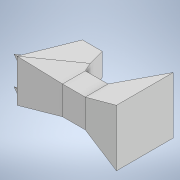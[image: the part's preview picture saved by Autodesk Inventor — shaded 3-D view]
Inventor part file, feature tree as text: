
AUTODESK INVENTOR PART (.ipt)
format: ipt  version: 2021 (Build 250183000, 183)  size: 184,320 bytes
history: native  units: in
note: dims shown in document units (in); Inventor stores cm internally (conversion verified against a paired STEP export)
features: sketch x5, extrude x3, plane x3, projected_geometry x2, loft x1, mirror x1
ambient origin geometry x8: Origin, YZ Plane, XZ Plane, XY Plane, X Axis, Y Axis, Z Axis, Center Point
bodies: Solid1 (feature_tree)
feature tree (15):
  extrude  "Extrusion1"  Depth=1.5748in
  extrude  "Extrusion2"  Depth=0.3937in
  plane  "Work Plane1"
  extrude  "Extrusion4"  Depth=1.0236in
  sketch  "Sketch5"  dims[d11=0.315in d12=0.1969in]
  plane  "Work Plane3"
  loft  "Loft3"
  plane  "Work Plane4"
  mirror  "Mirror1"
  sketch  "Sketch1"  dims[d1=1.5748in d2=0.7874in]
  sketch  "Sketch2"  dims[d7=0.3937in d8=1.4567in]
  projected_geometry  "Projected Loop1"
  sketch  "Sketch4"  dims[d9=0.2756in d10=1.0236in]
  projected_geometry  "Projected Loop2"
  sketch  "Sketch8"  dims[d13=0.7874in d14=0.0in d15=0.1969in d16=0.0984in d17=0.7874in d18=0.0in d19=-1.5748in d24=0.1181in d25=0.1181in d26=0.8661in d27=0.0in d33=0.0787in d42=0.1575in d53=0.0394in d55=0.0394in d56=0.0394in d57=0.0in d58=90.0deg d59=0.0in d60=90.0deg]
